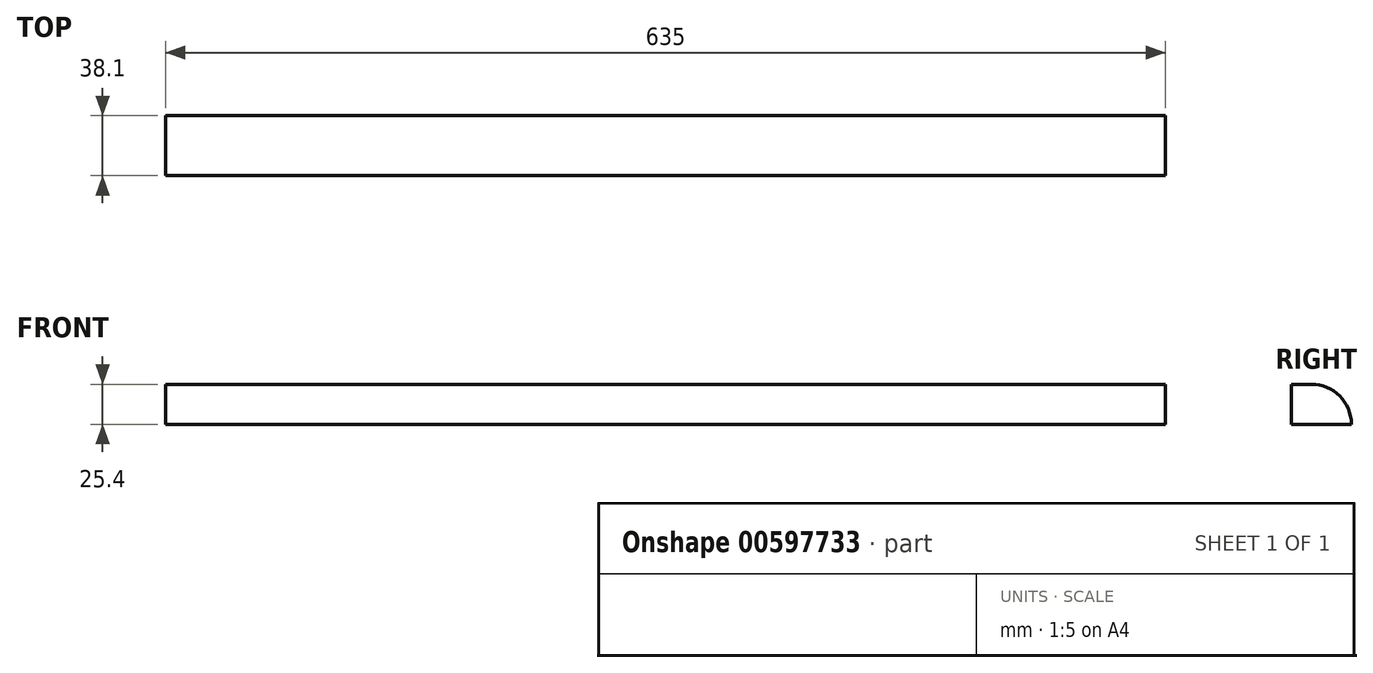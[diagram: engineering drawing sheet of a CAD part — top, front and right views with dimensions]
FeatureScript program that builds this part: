
annotation { "Feature Type Name" : "Feature", "Feature Type Description" : "" }
export const myFeature = defineFeature(function(context is Context, id is Id, definition is map)
    precondition{}
    {
        {
            var Q0;
            Q0=qCreatedBy(makeId("Right.planeOp"),FACE);
            var sketch = newSketch(context, id + "F0", { "sketchPlane" : qUnion([Q0])});
            skLineSegment(sketch, "E0.bottom", {"start": v(0, 0) * mm, "end": v(38.1, 0) * mm});
            skLineSegment(sketch, "E0.top", {"start": v(0, 25.4) * mm, "end": v(12.7, 25.4) * mm});
            skLineSegment(sketch, "E0.left", {"start": v(0, 0) * mm, "end": v(0, 25.4) * mm});
            skLineSegment(sketch, "E0.right", {"start": v(38.1, 0) * mm, "end": v(38.1, 0) * mm});
            skPoint(sketch, "E1.visualSharp", {"position": v(38.1, 25.4) * mm});
            skArc(sketch, "E1.filletArc", {"start": v(38.1, 0) * mm, "mid": v(30.66, 17.96) * mm, "end": v(12.7, 25.4) * mm});
            skSolve(sketch);
        }
        {
            var Q0;
            Q0 = qSketchRegion(id + "F0", true);
            extrude(context, id + "F1", {"entities" : qUnion([Q0]), "oppositeDirection" : true, "depth" : 635 * mm, "offsetDistance" : 25.4 * mm});
        }
    });
